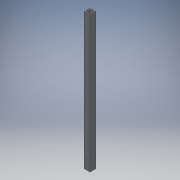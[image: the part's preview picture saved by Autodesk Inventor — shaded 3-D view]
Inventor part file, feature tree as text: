
AUTODESK INVENTOR PART (.ipt)
format: ipt  version: 2018 (Build 220112000, 112)  size: 140,288 bytes
history: native  units: in
note: dims shown in document units (in); Inventor stores cm internally (conversion verified against a paired STEP export)
features: extrude x4, sketch x4
ambient origin geometry x8: Origin, YZ Plane, XZ Plane, XY Plane, X Axis, Y Axis, Z Axis, Center Point
bodies: Solid1 (feature_tree)
feature tree (8):
  extrude  "Extrusion1"  Depth=1.0in
  sketch  "Sketch2"  dims[d2=0.125in d3=24.0in d4=0.0in]
  extrude  "Extrusion4"  Depth=24.0in TaperAngle=0.0deg
  extrude  "Extrusion5"  Depth=1.0in
  extrude  "Extrusion6"  Depth=1.0in
  sketch  "Sketch1"  dims[d0=1.0in d1=1.0in]
  sketch  "Sketch4"  dims[d5=0.5in d6=1.0in]
  sketch  "Sketch5"  dims[d7=0.5in d8=1.0in d9=0.2031in d10=0.2031in d19=0.5in d20=1.0in d21=0.2031in d22=0.2031in d23=5.0in d24=0.0in d25=0.382in d26=2.681in d27=0.26in d28=2.0in d29=0.0in d30=1.0in d31=0.2031in d32=1.0in d33=0.0in]
